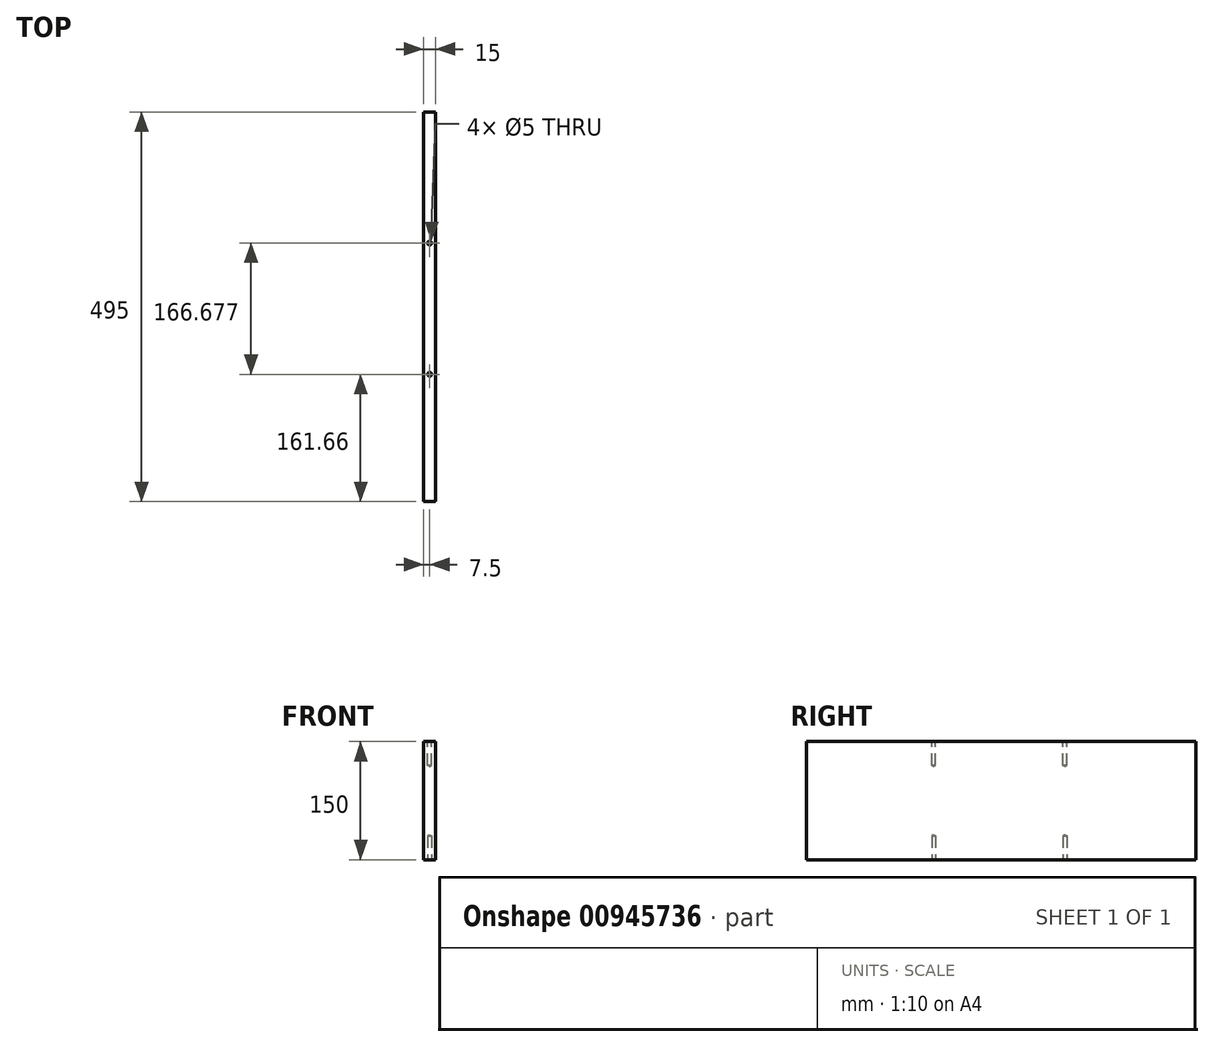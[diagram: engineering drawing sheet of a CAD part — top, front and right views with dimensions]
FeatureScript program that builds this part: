
annotation { "Feature Type Name" : "Feature", "Feature Type Description" : "" }
export const myFeature = defineFeature(function(context is Context, id is Id, definition is map)
    precondition{}
    {
        {
            var Q0;
            Q0=qCreatedBy(makeId("Right.planeOp"),FACE);
            var sketch = newSketch(context, id + "F0", { "sketchPlane" : qUnion([Q0])});
            skLineSegment(sketch, "E0.bottom", {"start": v(-247.5, 75) * mm, "end": v(247.5, 75) * mm});
            skLineSegment(sketch, "E0.top", {"start": v(-247.5, -75) * mm, "end": v(247.5, -75) * mm});
            skLineSegment(sketch, "E0.left", {"start": v(-247.5, 75) * mm, "end": v(-247.5, -75) * mm});
            skLineSegment(sketch, "E0.right", {"start": v(247.5, 75) * mm, "end": v(247.5, -75) * mm});
            skPoint(sketch, "E0.middle", {"position": v(0, 0) * mm});
            skSolve(sketch);
        }
        {
            var Q0;
            Q0=makeQuery(id+"F0.imprint","IMPRINT",FACE,{"disambiguationData":[TD([[makeQuery(id+"F0.imprint","IMPRINT",EDGE,{"derivedFrom":sQuery(id+"F0.wireOp",EDGE,"E0.bottom")}),-1.0]])]});
            extrude(context, id + "F1", {"entities" : qUnion([Q0]), "endBound" : BoundingType.SYMMETRIC, "depth" : 15 * mm, "offsetDistance" : 25 * mm});
        }
        {
            var Q0;
            Q0=makeQuery(id+"F1.opExtrude","SWEPT_FACE",FACE,{"disambiguationData":[OSD([sQuery(id+"F0.wireOp",EDGE,"E0.bottom")])]});
            var sketch = newSketch(context, id + "F2", { "sketchPlane" : qUnion([Q0])});
            skLineSegment(sketch, "E1", {"start": v(0, -247.5) * mm, "end": v(0, 247.5) * mm});
            skPoint(sketch, "E2", {"position": v(0, -85.83) * mm});
            skPoint(sketch, "E3", {"position": v(0, 80.84) * mm});
            skSolve(sketch);
        }
        {
            var Q0;
            Q0=makeQuery(id+"F1.opExtrude","SWEPT_FACE",FACE,{"disambiguationData":[OSD([sQuery(id+"F0.wireOp",EDGE,"E0.top")])]});
            var sketch = newSketch(context, id + "F3", { "sketchPlane" : qUnion([Q0])});
            skLineSegment(sketch, "E4", {"start": v(0, 247.5) * mm, "end": v(0, -247.5) * mm});
            skPoint(sketch, "E5", {"position": v(0, -80.83) * mm});
            skPoint(sketch, "E6", {"position": v(0, 85.84) * mm});
            skSolve(sketch);
        }
        {
            var Q0;
            Q0=sQuery(id+"F2.wireOp",VERTEX,"E3");
            var Q1;
            Q1=sQuery(id+"F2.wireOp",VERTEX,"E2");
            var Q2;
            Q2=sQuery(id+"F3.wireOp",VERTEX,"E6");
            var Q3;
            Q3=sQuery(id+"F3.wireOp",VERTEX,"E5");
            var Q4;
            Q4=makeQuery(id+"F1.opExtrude","SWEPT_BODY",BODY,{"disambiguationData":[OSD([sQuery(id+"F0.wireOp",EDGE,"E0.bottom"),sQuery(id+"F0.wireOp",EDGE,"E0.top"),sQuery(id+"F0.wireOp",EDGE,"E0.left"),sQuery(id+"F0.wireOp",EDGE,"E0.right")])]});
            hole(context, id + "F4", {"style" : HoleStyle.SIMPLE, "endStyle" : HoleEndStyle.BLIND, "holeDiameter" : 5 * mm, "majorDiameter" : 5 * mm, "holeDepth" : 30 * mm, "isTappedThrough" : true, "tappedDepth" : 12 * mm, "tapClearance" : 3, "locations" : qUnion([Q0, Q1, Q2, Q3]), "scope" : qUnion([Q4])});
        }
    });
